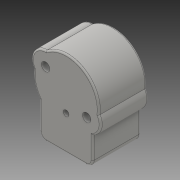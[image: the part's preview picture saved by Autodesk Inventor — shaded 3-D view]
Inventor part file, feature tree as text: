
AUTODESK INVENTOR PART (.ipt)
format: ipt  version: 2016 SP1 (Build 200210100, 210)  size: 225,280 bytes
history: native  units: mm
features: fillet x2, extrude x1, sketch x1, other x1
ambient origin geometry x8: Origin, YZ Plane, XZ Plane, XY Plane, X Axis, Y Axis, Z Axis, Center Point
bodies: Solid1 (feature_tree)
feature tree (5):
  extrude  "Extrusion1"  Depth=0.5mm
  fillet  "Fillet1"  Radius=16.637mm
  fillet  "Fillet2"  Radius=7.442mm
  sketch  "Sketch1"  dims[d0=26.908mm d1=21.748mm d2=16.637mm d3=7.442mm d21=2.642mm d22=1.778mm d23=15.0mm d24=0.0mm d26=2.0mm d27=0.5mm]
  other  "Image1"
